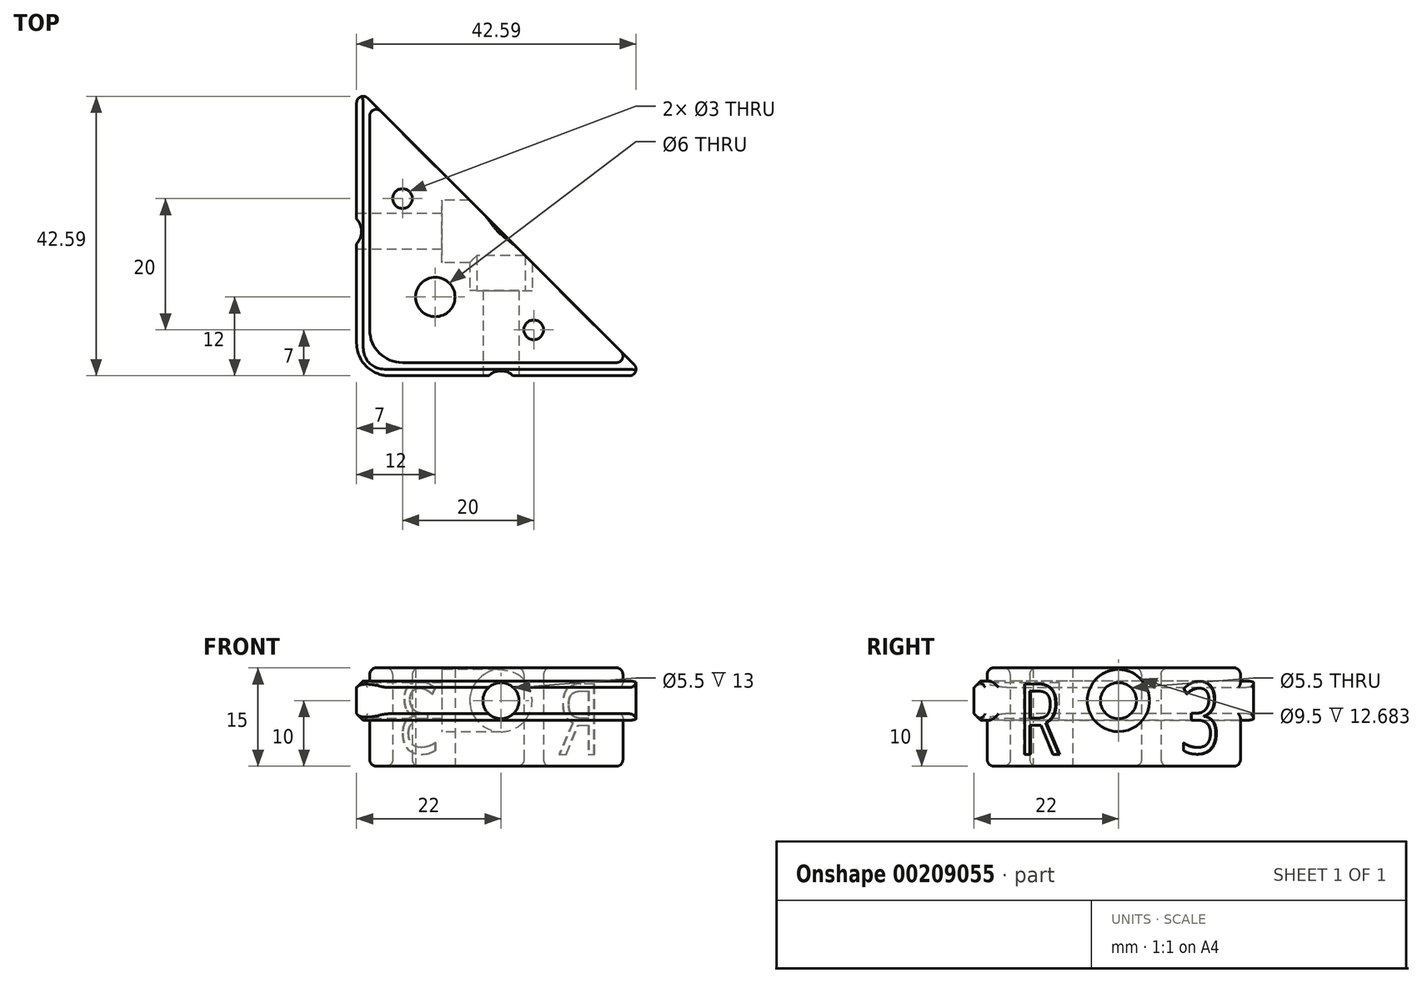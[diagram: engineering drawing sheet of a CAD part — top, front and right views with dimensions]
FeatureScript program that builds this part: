
annotation { "Feature Type Name" : "Feature", "Feature Type Description" : "" }
export const myFeature = defineFeature(function(context is Context, id is Id, definition is map)
    precondition{}
    {
        {
            var Q0;
            Q0=qCreatedBy(makeId("Top.planeOp"),FACE);
            var sketch = newSketch(context, id + "F0", { "sketchPlane" : qUnion([Q0])});
            skLineSegment(sketch, "E0", {"start": v(-5, 35) * mm, "end": v(-5, -5) * mm});
            skLineSegment(sketch, "E1", {"start": v(-5, -5) * mm, "end": v(35, -5) * mm});
            skLineSegment(sketch, "E2", {"start": v(35, -5) * mm, "end": v(-5, 35) * mm});
            skCircle(sketch, "E3", {"center": v(5, 5) * mm, "radius": 3 * mm});
            skLineSegment(sketch, "E4", {"start": v(-5, -5) * mm, "end": v(15, 15) * mm, "construction": true});
            skCircle(sketch, "E5", {"center": v(0, 20) * mm, "radius": 1.5 * mm});
            skCircle(sketch, "E6", {"center": v(20, 0) * mm, "radius": 1.5 * mm});
            skLineSegment(sketch, "E7", {"start": v(0, -5) * mm, "end": v(0, 30) * mm, "construction": true});
            skLineSegment(sketch, "E8", {"start": v(-5, 0) * mm, "end": v(30, 0) * mm, "construction": true});
            skLineSegment(sketch, "E9", {"start": v(-5, 35) * mm, "end": v(-7, 37) * mm});
            skLineSegment(sketch, "E10", {"start": v(-7, 37) * mm, "end": v(-7, -7) * mm});
            skLineSegment(sketch, "E11", {"start": v(-7, -7) * mm, "end": v(37, -7) * mm});
            skLineSegment(sketch, "E12", {"start": v(37, -7) * mm, "end": v(35, -5) * mm});
            skLineSegment(sketch, "E13", {"start": v(-7, 37) * mm, "end": v(37, -7) * mm, "construction": true});
            skPoint(sketch, "E14", {"position": v(0, 11.38) * mm});
            skLineSegment(sketch, "E15", {"start": v(0, 20) * mm, "end": v(20, 0) * mm, "construction": true});
            skSolve(sketch);
        }
        {
            var Q0;
            Q0=makeQuery(id+"F0.imprint","IMPRINT",FACE,{"disambiguationData":[TD([[makeQuery(id+"F0.imprint","IMPRINT",EDGE,{"derivedFrom":sQuery(id+"F0.wireOp",EDGE,"E0")}),1.0]])]});
            extrude(context, id + "F1", {"entities" : qUnion([Q0]), "depth" : 15 * mm});
        }
        {
            var Q0;
            Q0=makeQuery(id+"F0.imprint","IMPRINT",FACE,{"disambiguationData":[TD([[makeQuery(id+"F0.imprint","IMPRINT",EDGE,{"derivedFrom":sQuery(id+"F0.wireOp",EDGE,"E0")}),-1.0]])]});
            extrude(context, id + "F2", {"entities" : qUnion([Q0]), "operationType" : NewBodyOperationType.ADD, "depth" : 13 * mm, "hasSecondDirection" : true, "secondDirectionOppositeDirection" : false, "secondDirectionDepth" : 7 * mm});
        }
        {
            var Q0;
            Q0=makeQuery(id+"F2.opExtrude","SWEPT_FACE",FACE,{"disambiguationData":[OSD([sQuery(id+"F0.wireOp",EDGE,"E11")])]});
            var sketch = newSketch(context, id + "F3", { "sketchPlane" : qUnion([Q0])});
            skPoint(sketch, "E16", {"position": v(15, 13) * mm});
            skCircle(sketch, "E17", {"center": v(15, 10) * mm, "radius": 2.75 * mm});
            skCircle(sketch, "E18", {"center": v(15, 10) * mm, "radius": 4.75 * mm});
            skSolve(sketch);
        }
        {
            var Q0;
            Q0=makeQuery(id+"F3.imprint","IMPRINT",FACE,{"disambiguationData":[TD([[makeQuery(id+"F3.imprint","IMPRINT",EDGE,{"derivedFrom":sQuery(id+"F3.wireOp",EDGE,"E17")}),1.0]])]});
            extrude(context, id + "F4", {"entities" : qUnion([Q0]), "operationType" : NewBodyOperationType.REMOVE, "endBound" : BoundingType.THROUGH_ALL, "oppositeDirection" : true, "depth" : 25 * mm});
        }
        {
            var Q0;
            Q0=makeQuery(id+"F3.imprint","IMPRINT",FACE,{"disambiguationData":[TD([[makeQuery(id+"F3.imprint","IMPRINT",EDGE,{"derivedFrom":sQuery(id+"F3.wireOp",EDGE,"E17")}),-1.0]])]});
            var Q1;
            {var subQ0=sQuery(id+"F3.wireOp",EDGE,"E18");var subQ1=makeQuery(id+"F2.opExtrude","CAP_EDGE",EDGE,{"disambiguationData":[OSD([sQuery(id+"F0.wireOp",EDGE,"E11")])],"isStart":false});var subQ2=makeQuery(id+"F3.imprint","INTERSECT",VERTEX,{"disambiguationData":[OD(0.0)],"derivedFrom":[subQ1,subQ0]});Q1=makeQuery(id+"F3.imprint","IMPRINT",FACE,{"disambiguationData":[TD([[makeQuery(id+"F3.imprint","IMPRINT",EDGE,{"disambiguationData":[TD([[subQ2,1.0]])],"derivedFrom":subQ0}),1.0]])]});}
            var Q2;
            {var subQ0=sQuery(id+"F3.wireOp",EDGE,"E18");var subQ1=makeQuery(id+"F2.opExtrude","CAP_EDGE",EDGE,{"disambiguationData":[OSD([sQuery(id+"F0.wireOp",EDGE,"E11")])],"isStart":true});var subQ2=makeQuery(id+"F3.imprint","INTERSECT",VERTEX,{"disambiguationData":[OD(0.0)],"derivedFrom":[subQ1,subQ0]});Q2=makeQuery(id+"F3.imprint","IMPRINT",FACE,{"disambiguationData":[TD([[makeQuery(id+"F3.imprint","IMPRINT",EDGE,{"disambiguationData":[TD([[subQ2,-1.0]])],"derivedFrom":subQ0}),1.0]])]});}
            extrude(context, id + "F5", {"entities" : qUnion([Q0, Q1, Q2]), "operationType" : NewBodyOperationType.REMOVE, "endBound" : BoundingType.THROUGH_ALL, "oppositeDirection" : true, "depth" : 32.06 * mm, "hasSecondDirection" : true, "secondDirectionOppositeDirection" : true, "secondDirectionDepth" : 13 * mm});
        }
        {
            var Q0;
            Q0=makeQuery(id+"F2.opExtrude","SWEPT_FACE",FACE,{"disambiguationData":[OSD([sQuery(id+"F0.wireOp",EDGE,"E10")])]});
            var sketch = newSketch(context, id + "F6", { "sketchPlane" : qUnion([Q0])});
            skPoint(sketch, "E19.centerSnap0", {"position": v(-15, 13) * mm});
            skCircle(sketch, "E20", {"center": v(-15, 10) * mm, "radius": 2.75 * mm});
            skCircle(sketch, "E21", {"center": v(-15, 10) * mm, "radius": 4.75 * mm});
            skSolve(sketch);
        }
        {
            var Q0;
            Q0=makeQuery(id+"F6.imprint","IMPRINT",FACE,{"disambiguationData":[TD([[makeQuery(id+"F6.imprint","IMPRINT",EDGE,{"derivedFrom":sQuery(id+"F6.wireOp",EDGE,"E20")}),1.0]])]});
            extrude(context, id + "F7", {"entities" : qUnion([Q0]), "operationType" : NewBodyOperationType.REMOVE, "endBound" : BoundingType.THROUGH_ALL, "oppositeDirection" : true, "depth" : 25 * mm});
        }
        {
            var Q0;
            {var subQ0=sQuery(id+"F6.wireOp",EDGE,"E21");var subQ1=makeQuery(id+"F2.opExtrude","CAP_EDGE",EDGE,{"disambiguationData":[OSD([sQuery(id+"F0.wireOp",EDGE,"E10")])],"isStart":false});var subQ2=makeQuery(id+"F6.imprint","INTERSECT",VERTEX,{"disambiguationData":[OD(0.0)],"derivedFrom":[subQ1,subQ0]});Q0=makeQuery(id+"F6.imprint","IMPRINT",FACE,{"disambiguationData":[TD([[makeQuery(id+"F6.imprint","IMPRINT",EDGE,{"disambiguationData":[TD([[subQ2,1.0]])],"derivedFrom":subQ0}),1.0]])]});}
            var Q1;
            Q1=makeQuery(id+"F6.imprint","IMPRINT",FACE,{"disambiguationData":[TD([[makeQuery(id+"F6.imprint","IMPRINT",EDGE,{"derivedFrom":sQuery(id+"F6.wireOp",EDGE,"E20")}),-1.0]])]});
            var Q2;
            {var subQ0=sQuery(id+"F6.wireOp",EDGE,"E21");var subQ1=makeQuery(id+"F2.opExtrude","CAP_EDGE",EDGE,{"disambiguationData":[OSD([sQuery(id+"F0.wireOp",EDGE,"E10")])],"isStart":true});var subQ2=makeQuery(id+"F6.imprint","INTERSECT",VERTEX,{"disambiguationData":[OD(0.0)],"derivedFrom":[subQ1,subQ0]});Q2=makeQuery(id+"F6.imprint","IMPRINT",FACE,{"disambiguationData":[TD([[makeQuery(id+"F6.imprint","IMPRINT",EDGE,{"disambiguationData":[TD([[subQ2,-1.0]])],"derivedFrom":subQ0}),1.0]])]});}
            extrude(context, id + "F8", {"entities" : qUnion([Q0, Q1, Q2]), "operationType" : NewBodyOperationType.REMOVE, "endBound" : BoundingType.THROUGH_ALL, "oppositeDirection" : true, "depth" : 25 * mm, "hasSecondDirection" : true, "secondDirectionOppositeDirection" : true, "secondDirectionDepth" : 13 * mm});
        }
        {
            var Q0;
            Q0=makeQuery(id+"F2.opExtrude","CAP_EDGE",EDGE,{"disambiguationData":[OSD([sQuery(id+"F0.wireOp",EDGE,"E10")])],"isStart":true});
            var Q1;
            Q1=makeQuery(id+"F2.opExtrude","CAP_EDGE",EDGE,{"disambiguationData":[OSD([sQuery(id+"F0.wireOp",EDGE,"E10")])],"isStart":false});
            var Q2;
            Q2=makeQuery(id+"F2.opExtrude","CAP_EDGE",EDGE,{"disambiguationData":[OSD([sQuery(id+"F0.wireOp",EDGE,"E11")])],"isStart":false});
            var Q3;
            Q3=makeQuery(id+"F2.opExtrude","CAP_EDGE",EDGE,{"disambiguationData":[OSD([sQuery(id+"F0.wireOp",EDGE,"E11")])],"isStart":true});
            chamfer(context, id + "F9", {"entities" : qUnion([Q0, Q1, Q2, Q3]), "width" : 1 * mm, "tangentPropagation" : true});
        }
        {
            var Q0;
            Q0=makeQuery(id+"F1.opExtrude","CAP_EDGE",EDGE,{"disambiguationData":[OSD([sQuery(id+"F0.wireOp",EDGE,"E5")])],"isStart":true});
            var Q1;
            Q1=makeQuery(id+"F1.opExtrude","CAP_EDGE",EDGE,{"disambiguationData":[OSD([sQuery(id+"F0.wireOp",EDGE,"GBnq9T9O-Cd2u-0YYD-0rPR-wLLdpOveml1q")])],"isStart":true});
            var Q2;
            Q2=makeQuery(id+"F1.opExtrude","CAP_EDGE",EDGE,{"disambiguationData":[OSD([sQuery(id+"F0.wireOp",EDGE,"LA5ZwjMC-8dX6-lRKu-0FuP-NofH7RVELHak")])],"isStart":true});
            var Q3;
            Q3=makeQuery(id+"F1.opExtrude","CAP_EDGE",EDGE,{"disambiguationData":[OSD([sQuery(id+"F0.wireOp",EDGE,"zmZg36L2-PVC0-XoSg-Sp8r-rVE9DayIcdcC")])],"isStart":true});
            var Q4;
            Q4=makeQuery(id+"F1.opExtrude","CAP_EDGE",EDGE,{"disambiguationData":[OSD([sQuery(id+"F0.wireOp",EDGE,"E6")])],"isStart":true});
            var Q5;
            Q5=makeQuery(id+"F1.opExtrude","CAP_EDGE",EDGE,{"disambiguationData":[OSD([sQuery(id+"F0.wireOp",EDGE,"E6")])],"isStart":false});
            var Q6;
            Q6=makeQuery(id+"F1.opExtrude","CAP_EDGE",EDGE,{"disambiguationData":[OSD([sQuery(id+"F0.wireOp",EDGE,"GBnq9T9O-Cd2u-0YYD-0rPR-wLLdpOveml1q")])],"isStart":false});
            var Q7;
            Q7=makeQuery(id+"F1.opExtrude","CAP_EDGE",EDGE,{"disambiguationData":[OSD([sQuery(id+"F0.wireOp",EDGE,"E5")])],"isStart":false});
            var Q8;
            Q8=makeQuery(id+"F1.opExtrude","CAP_EDGE",EDGE,{"disambiguationData":[OSD([sQuery(id+"F0.wireOp",EDGE,"zmZg36L2-PVC0-XoSg-Sp8r-rVE9DayIcdcC")])],"isStart":false});
            var Q9;
            Q9=makeQuery(id+"F1.opExtrude","SWEPT_FACE",FACE,{"disambiguationData":[OSD([sQuery(id+"F0.wireOp",EDGE,"LA5ZwjMC-8dX6-lRKu-0FuP-NofH7RVELHak")])]});
            fillet(context, id + "F10", {"entities" : qUnion([Q0, Q1, Q2, Q3, Q4, Q5, Q6, Q7, Q8, Q9]), "radius" : 1 * mm, "tangentPropagation" : true, "allowEdgeOverflow" : false});
        }
        {
            var Q0;
            {var subQ0=sQuery(id+"F0.wireOp",EDGE,"E0");var subQ1=sQuery(id+"F0.wireOp",EDGE,"E1");Q0=makeQuery(id+"F2.boolean.opBoolean","SPLIT",EDGE,{"disambiguationData":[TD([makeQuery(id+"F2.opExtrude","CAP_FACE",FACE,{"disambiguationData":[OSD([subQ0,subQ1,sQuery(id+"F0.wireOp",EDGE,"E9"),sQuery(id+"F0.wireOp",EDGE,"E10"),sQuery(id+"F0.wireOp",EDGE,"E11"),sQuery(id+"F0.wireOp",EDGE,"E12")])],"isStart":true})])],"derivedFrom":makeQuery(id+"F1.opExtrude","SWEPT_EDGE",EDGE,{"disambiguationData":[OSD([subQ0,subQ1])]})});}
            var Q1;
            {var subQ0=sQuery(id+"F0.wireOp",EDGE,"E0");var subQ1=sQuery(id+"F0.wireOp",EDGE,"E1");Q1=makeQuery(id+"F2.boolean.opBoolean","SPLIT",EDGE,{"disambiguationData":[TD([makeQuery(id+"F2.opExtrude","CAP_FACE",FACE,{"disambiguationData":[OSD([subQ0,subQ1,sQuery(id+"F0.wireOp",EDGE,"E9"),sQuery(id+"F0.wireOp",EDGE,"E10"),sQuery(id+"F0.wireOp",EDGE,"E11"),sQuery(id+"F0.wireOp",EDGE,"E12")])],"isStart":false})])],"derivedFrom":makeQuery(id+"F1.opExtrude","SWEPT_EDGE",EDGE,{"disambiguationData":[OSD([subQ0,subQ1])]})});}
            var Q2;
            Q2=makeQuery(id+"F9.opChamfer","BLEND_EDGE",EDGE,{"blendedFrom":[makeQuery(id+"F2.opExtrude","CAP_EDGE",EDGE,{"disambiguationData":[OSD([sQuery(id+"F0.wireOp",EDGE,"E10")])],"isStart":false}),makeQuery(id+"F2.opExtrude","CAP_EDGE",EDGE,{"disambiguationData":[OSD([sQuery(id+"F0.wireOp",EDGE,"E11")])],"isStart":false})],"blendedInto":[]});
            var Q3;
            Q3=makeQuery(id+"F2.opExtrude","SWEPT_EDGE",EDGE,{"disambiguationData":[OSD([sQuery(id+"F0.wireOp",EDGE,"E10"),sQuery(id+"F0.wireOp",EDGE,"E11")])]});
            var Q4;
            Q4=makeQuery(id+"F9.opChamfer","BLEND_EDGE",EDGE,{"blendedFrom":[makeQuery(id+"F2.opExtrude","CAP_EDGE",EDGE,{"disambiguationData":[OSD([sQuery(id+"F0.wireOp",EDGE,"E10")])],"isStart":true}),makeQuery(id+"F2.opExtrude","CAP_EDGE",EDGE,{"disambiguationData":[OSD([sQuery(id+"F0.wireOp",EDGE,"E11")])],"isStart":true})],"blendedInto":[]});
            fillet(context, id + "F11", {"entities" : qUnion([Q0, Q1, Q2, Q3, Q4]), "radius" : 5 * mm, "tangentPropagation" : true, "allowEdgeOverflow" : false});
        }
        {
            var Q0;
            Q0=makeQuery(id+"F1.opExtrude","CAP_EDGE",EDGE,{"disambiguationData":[OSD([sQuery(id+"F0.wireOp",EDGE,"E2")])],"isStart":true});
            var Q1;
            Q1=makeQuery(id+"F1.opExtrude","CAP_EDGE",EDGE,{"disambiguationData":[OSD([sQuery(id+"F0.wireOp",EDGE,"E2")])],"isStart":false});
            var Q2;
            {var subQ0=sQuery(id+"F0.wireOp",EDGE,"E12");var subQ1=sQuery(id+"F0.wireOp",EDGE,"E9");var subQ2=sQuery(id+"F0.wireOp",EDGE,"E1");var subQ3=sQuery(id+"F0.wireOp",EDGE,"E0");var subQ4=sQuery(id+"F0.wireOp",EDGE,"E2");Q2=makeQuery(id+"F2.boolean.opBoolean","SPLIT",EDGE,{"disambiguationData":[TD([makeQuery(id+"F2.opExtrude","CAP_FACE",FACE,{"disambiguationData":[OSD([subQ3,subQ2,subQ1,sQuery(id+"F0.wireOp",EDGE,"E10"),sQuery(id+"F0.wireOp",EDGE,"E11"),subQ0])],"isStart":false})])],"derivedFrom":makeQuery(id+"F1.opExtrude","SWEPT_EDGE",EDGE,{"disambiguationData":[OSD([subQ2,subQ4,subQ0])]})});}
            var Q3;
            Q3=makeQuery(id+"F2.opExtrude","SWEPT_EDGE",EDGE,{"disambiguationData":[OSD([sQuery(id+"F0.wireOp",EDGE,"E11"),sQuery(id+"F0.wireOp",EDGE,"E12")])]});
            var Q4;
            {var subQ0=sQuery(id+"F0.wireOp",EDGE,"E12");var subQ1=sQuery(id+"F0.wireOp",EDGE,"E9");var subQ2=sQuery(id+"F0.wireOp",EDGE,"E1");var subQ3=sQuery(id+"F0.wireOp",EDGE,"E0");var subQ4=sQuery(id+"F0.wireOp",EDGE,"E2");Q4=makeQuery(id+"F2.boolean.opBoolean","SPLIT",EDGE,{"disambiguationData":[TD([makeQuery(id+"F2.opExtrude","CAP_FACE",FACE,{"disambiguationData":[OSD([subQ3,subQ2,subQ1,sQuery(id+"F0.wireOp",EDGE,"E10"),sQuery(id+"F0.wireOp",EDGE,"E11"),subQ0])],"isStart":true})])],"derivedFrom":makeQuery(id+"F1.opExtrude","SWEPT_EDGE",EDGE,{"disambiguationData":[OSD([subQ2,subQ4,subQ0])]})});}
            var Q5;
            {var subQ0=sQuery(id+"F0.wireOp",EDGE,"E12");var subQ1=sQuery(id+"F0.wireOp",EDGE,"E9");var subQ2=sQuery(id+"F0.wireOp",EDGE,"E1");var subQ3=sQuery(id+"F0.wireOp",EDGE,"E0");var subQ4=sQuery(id+"F0.wireOp",EDGE,"E2");Q5=makeQuery(id+"F2.boolean.opBoolean","SPLIT",EDGE,{"disambiguationData":[TD([makeQuery(id+"F2.opExtrude","CAP_FACE",FACE,{"disambiguationData":[OSD([subQ3,subQ2,subQ1,sQuery(id+"F0.wireOp",EDGE,"E10"),sQuery(id+"F0.wireOp",EDGE,"E11"),subQ0])],"isStart":true})])],"derivedFrom":makeQuery(id+"F1.opExtrude","SWEPT_EDGE",EDGE,{"disambiguationData":[OSD([subQ3,subQ4,subQ1])]})});}
            var Q6;
            {var subQ0=sQuery(id+"F0.wireOp",EDGE,"E12");var subQ1=sQuery(id+"F0.wireOp",EDGE,"E9");var subQ2=sQuery(id+"F0.wireOp",EDGE,"E1");var subQ3=sQuery(id+"F0.wireOp",EDGE,"E0");var subQ4=sQuery(id+"F0.wireOp",EDGE,"E2");Q6=makeQuery(id+"F2.boolean.opBoolean","SPLIT",EDGE,{"disambiguationData":[TD([makeQuery(id+"F2.opExtrude","CAP_FACE",FACE,{"disambiguationData":[OSD([subQ3,subQ2,subQ1,sQuery(id+"F0.wireOp",EDGE,"E10"),sQuery(id+"F0.wireOp",EDGE,"E11"),subQ0])],"isStart":false})])],"derivedFrom":makeQuery(id+"F1.opExtrude","SWEPT_EDGE",EDGE,{"disambiguationData":[OSD([subQ3,subQ4,subQ1])]})});}
            var Q7;
            Q7=makeQuery(id+"F2.opExtrude","SWEPT_EDGE",EDGE,{"disambiguationData":[OSD([sQuery(id+"F0.wireOp",EDGE,"E9"),sQuery(id+"F0.wireOp",EDGE,"E10")])]});
            var Q8;
            Q8=makeQuery(id+"F2.opExtrude","CAP_EDGE",EDGE,{"disambiguationData":[OSD([sQuery(id+"F0.wireOp",EDGE,"E12")])],"isStart":true});
            var Q9;
            Q9=makeQuery(id+"F2.opExtrude","CAP_EDGE",EDGE,{"disambiguationData":[OSD([sQuery(id+"F0.wireOp",EDGE,"E12")])],"isStart":false});
            var Q10;
            Q10=makeQuery(id+"F2.opExtrude","CAP_EDGE",EDGE,{"disambiguationData":[OSD([sQuery(id+"F0.wireOp",EDGE,"E9")])],"isStart":true});
            var Q11;
            Q11=makeQuery(id+"F2.opExtrude","CAP_EDGE",EDGE,{"disambiguationData":[OSD([sQuery(id+"F0.wireOp",EDGE,"E9")])],"isStart":false});
            var Q12;
            Q12=makeQuery(id+"F8.boolean.opBoolean","SPLIT",EDGE,{"disambiguationData":[OD(1.0)],"derivedFrom":makeQuery(id+"F5.boolean.opBoolean","INTERSECT",EDGE,{"derivedFrom":[makeQuery(id+"F2.boolean.opBoolean","MERGE",FACE,{"derivedFrom":[makeQuery(id+"F1.opExtrude","SWEPT_FACE",FACE,{"disambiguationData":[OSD([sQuery(id+"F0.wireOp",EDGE,"E2")])]}),makeQuery(id+"F2.opExtrude","SWEPT_FACE",FACE,{"disambiguationData":[OSD([sQuery(id+"F0.wireOp",EDGE,"E9")])]}),makeQuery(id+"F2.opExtrude","SWEPT_FACE",FACE,{"disambiguationData":[OSD([sQuery(id+"F0.wireOp",EDGE,"E12")])]})]}),makeQuery(id+"F5.opExtrude","SWEPT_FACE",FACE,{"disambiguationData":[OSD([sQuery(id+"F3.wireOp",EDGE,"DbkietmO-DzfW-C8Fo-o7GA-QJ81dBEigqW8")])]})]})});
            var Q13;
            Q13=makeQuery(id+"F8.boolean.opBoolean","SPLIT",EDGE,{"disambiguationData":[OD(0.0)],"derivedFrom":makeQuery(id+"F5.boolean.opBoolean","INTERSECT",EDGE,{"derivedFrom":[makeQuery(id+"F2.boolean.opBoolean","MERGE",FACE,{"derivedFrom":[makeQuery(id+"F1.opExtrude","SWEPT_FACE",FACE,{"disambiguationData":[OSD([sQuery(id+"F0.wireOp",EDGE,"E2")])]}),makeQuery(id+"F2.opExtrude","SWEPT_FACE",FACE,{"disambiguationData":[OSD([sQuery(id+"F0.wireOp",EDGE,"E9")])]}),makeQuery(id+"F2.opExtrude","SWEPT_FACE",FACE,{"disambiguationData":[OSD([sQuery(id+"F0.wireOp",EDGE,"E12")])]})]}),makeQuery(id+"F5.opExtrude","SWEPT_FACE",FACE,{"disambiguationData":[OSD([sQuery(id+"F3.wireOp",EDGE,"DbkietmO-DzfW-C8Fo-o7GA-QJ81dBEigqW8")])]})]})});
            var Q14;
            Q14=makeQuery(id+"F8.boolean.opBoolean","INTERSECT",EDGE,{"derivedFrom":[makeQuery(id+"F5.boolean.opBoolean","COPY",FACE,{"derivedFrom":makeQuery(id+"F5.opExtrude","SWEPT_FACE",FACE,{"disambiguationData":[OSD([sQuery(id+"F3.wireOp",EDGE,"DbkietmO-DzfW-C8Fo-o7GA-QJ81dBEigqW8")])]})}),makeQuery(id+"F8.opExtrude","SWEPT_FACE",FACE,{"disambiguationData":[OSD([sQuery(id+"F6.wireOp",EDGE,"pOpG8Zqg-zBgg-ELml-ohQh-qQ13d8d3ZW7T")])]})]});
            fillet(context, id + "F12", {"entities" : qUnion([Q0, Q1, Q2, Q3, Q4, Q5, Q6, Q7, Q8, Q9, Q10, Q11, Q12, Q13, Q14]), "radius" : 1 * mm, "tangentPropagation" : true, "allowEdgeOverflow" : false});
        }
        {
            var Q0;
            Q0=makeQuery(id+"F2.boolean.opBoolean","MERGE",FACE,{"derivedFrom":[makeQuery(id+"F1.opExtrude","SWEPT_FACE",FACE,{"disambiguationData":[OSD([sQuery(id+"F0.wireOp",EDGE,"E2")])]}),makeQuery(id+"F2.opExtrude","SWEPT_FACE",FACE,{"disambiguationData":[OSD([sQuery(id+"F0.wireOp",EDGE,"E9")])]}),makeQuery(id+"F2.opExtrude","SWEPT_FACE",FACE,{"disambiguationData":[OSD([sQuery(id+"F0.wireOp",EDGE,"E12")])]})]});
            var sketch = newSketch(context, id + "F13", { "sketchPlane" : qUnion([Q0])});
            skPoint(sketch, "E22", {"position": v(25.87, 13) * mm});
            skText(sketch, "E23", { "text": "R", "fontName": "OpenSans-Regular.ttf"});
            skText(sketch, "E24", { "text": "3", "fontName": "OpenSans-Regular.ttf"});
            skPoint(sketch, "E25", {"position": v(-16.36, 14) * mm});
            const initialGuessF13  = {"E23": [-0.02168, 0.00182, 1, 0, 0.01081], "E24": [0.01334, 0.00198, 1, 0, 0.0109]};
            skSetInitialGuess(sketch, initialGuessF13);
            skSolve(sketch);
        }
        {
            var Q0;
            Q0=qSketchRegion(id+"F13",true);
            extrude(context, id + "F14", {"entities" : qUnion([Q0]), "operationType" : NewBodyOperationType.REMOVE, "oppositeDirection" : true, "depth" : .15 * mm});
        }
        {
            var Q0;
            Q0=makeQuery(id+"F1.opExtrude","CAP_EDGE",EDGE,{"disambiguationData":[OSD([sQuery(id+"F0.wireOp",EDGE,"E0")])],"isStart":true});
            var Q1;
            Q1=makeQuery(id+"F1.opExtrude","CAP_EDGE",EDGE,{"disambiguationData":[OSD([sQuery(id+"F0.wireOp",EDGE,"E0")])],"isStart":false});
            fillet(context, id + "F15", {"entities" : qUnion([Q0, Q1]), "radius" : 1 * mm, "tangentPropagation" : true, "allowEdgeOverflow" : false});
        }
    });
